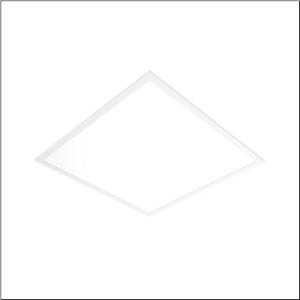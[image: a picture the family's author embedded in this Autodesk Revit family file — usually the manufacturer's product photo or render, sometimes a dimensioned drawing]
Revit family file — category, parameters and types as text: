
# Revit family: apollon_r__41_51mh11wd2443_7c66
name_source: partatom
category: Lighting Fixtures
units: mm (PartAtom-declared; Revit-internal decimal feet)

## family parameters
Cut with Voids When Loaded = No
Host = Face
Light Source = No
Part Type = Normal
Room Calculation Point = No
Round Connector Dimension = Use Diameter
Shared = No

## types (1)
- Apollon® 41 (1 x LED, 3500 lm, 28.5 W, 4000K)
    Apparent Load = 29 VA
    CIE Flux Codes = 61 87 97 100 100
    Color Rendering = 80
    Color Temperature = 4000K
    Default Elevation = 1800 mm
    Description = Apollon® 41, office luminaire, primary optical cover: prismatic diffuser, of PS, light emission: direct distribution, primary light characteristic: symmetric, installation type: lay-in mounting, LED, rated luminous flux: 3.500lm, luminous efficacy: 123lm/W, light colour: 840, colour temperature: 4000K, with terminal, 5-pole, mains connection: 220..240V, AC/DC, 0/50..60Hz, housing, of aluminium section, traffic white (RAL 9016), module: M625, length: 620mm, width: 620mm, height: 28mm, housing upper side, of sheet steel, protection rating (complete): IP20, protection rating (lamp compartment, on room side): IP40, insulation class (complete): insulation class II (safety insulation), certification: CE, ENEC, permissible operating ambient temperature: -25..+40°C, packaging unit: 1 piece
    Height = 0 mm  [stored 0 ft]
    Lamp = 1 x LED
    Lamp Light Flux = 3500 lm
    Lamp Power = 28.5 W
    Lamp count = 1
    Length = 620 mm
    Luminous efficacy = 123 lm/W
    Manufacturer = Siteco
    ModVariant = No
    Model = 51MH11WD2443
    Mounting Place = Ceiling
    Mounting Type = Recessed
    Number of Poles = 1
    OnlyDefault = Yes
    Power Factor = 1
    Product Name = Apollon® 41
    Product group = office luminaire | ceiling recessed
    ProductGroupID = 401
    Protection Class = Protection class II
    Protection Degree = IP 20
    RLX_Detail_Level = 1
    RLX_Emergency_Light_Flux = 0 lm
    RLX_Emergency_Type = 0
    RLX_Emergency_Type_DB = No
    RlxData = <blob elided: 12189 chars, md5=9ab818f9>
    Socket = socket
    Standby Power = 0 W
    System Light Flux = 3500 lm
    System Power = 29 W
    Type Comments = Product without accessories
    Type Image = l_1291024.jpg
    URL = http://relux.com
    VarID = ---
    Voltage = 0 V
    Weight = 0.00 kg
    Width = 620 mm

note: [stored X ft] marks values corroborated as IEEE doubles in the binary element streams (Revit-internal decimal feet)

## geometry (parser evidence)
native form markers: Sweep x8
no freeform markers — native parametric forms only
